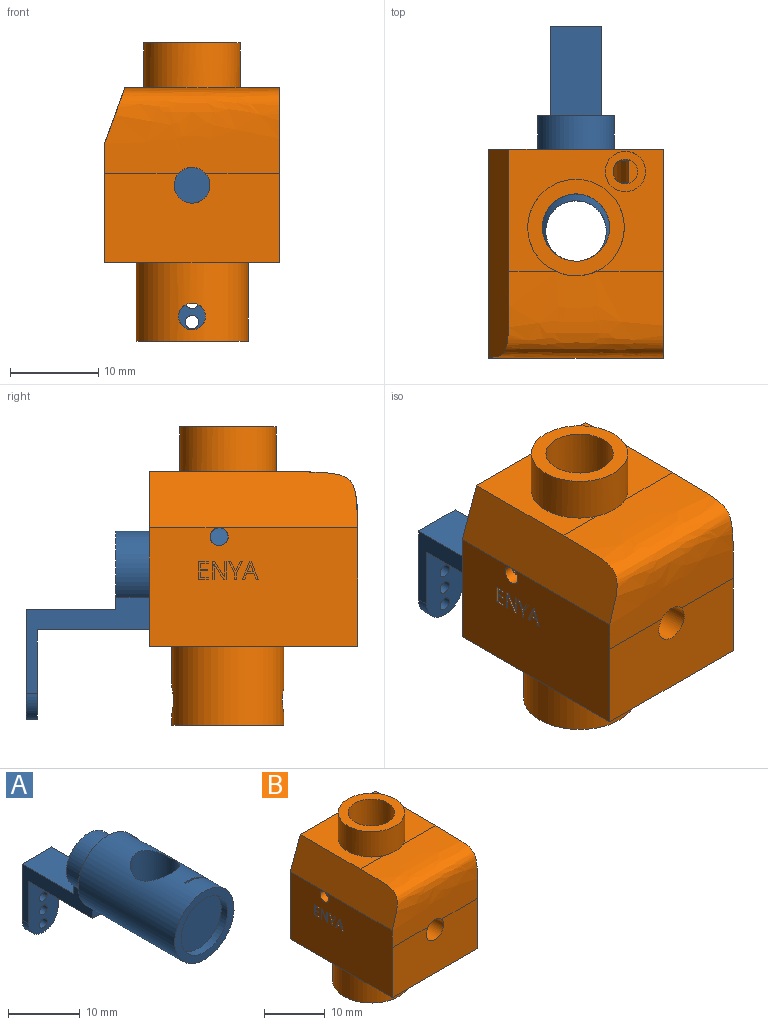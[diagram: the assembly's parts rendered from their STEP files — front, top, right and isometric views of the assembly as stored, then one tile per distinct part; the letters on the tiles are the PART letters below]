
ASSEMBLY  parts=2 mates=1
PART A: 29 faces, bbox 11.7x33x22.9 mm
  f0: cylinder r=4.32mm len=8.64mm, axis (0,-1,0), area 78.9mm2, adj f1,f17,f24,f25
  f1: plane 11.68x10.9mm, normal (0,1,0), area 39.1mm2, adj f0,f16,f24,f25
  f2: plane 11.68x11.68mm, normal (0,-1,0), area 41.6mm2, adj f3,f16
  f3: cylinder r=4.57mm len=9.14mm, axis (0,-1,0), area 36.5mm2, adj f2,f4
  f4: plane 9.14x9.14mm, normal (0,-1,0), area 65.7mm2, adj f3
  f5: cylinder r=3.43mm len=11.68mm, axis (0,0,1), area 228.4mm2, adj f16
  f6: plane 9.64x2.54mm, normal (0,-1,0), area 17.2mm2, adj f8,f16
  f7: plane 9.64x2.54mm, normal (0,1,0), area 17.2mm2, adj f8,f16
  f8: plane 9.64x2.54mm, normal (1,0,0), area 24.5mm2, adj f6,f7,f16
  f9: plane 6.21x4.58mm, normal (0,-1,0), area 21.8mm2, adj f10,f15,f16
  f10: cylinder r=1.27mm len=6.35mm, axis (1,0,0), area 23.5mm2, adj f9,f11,f15,f16
  f11: plane 6.21x4.58mm, normal (0,-1,0), area 21.8mm2, adj f10,f15,f16
  f12: plane 6.21x4.58mm, normal (0,1,0), area 21.8mm2, adj f13,f15,f16
  f13: cylinder r=1.27mm len=6.35mm, axis (1,0,0), area 23.5mm2, adj f12,f14,f15,f16
  f14: plane 6.21x4.58mm, normal (0,1,0), area 21.8mm2, adj f13,f15,f16
  f15: plane 11.64x2.54mm, normal (1,0,0), area 7.4mm2, adj f9,f10,f11,f12,f13,f14,f16
  f16: cylinder r=5.84mm len=19.05mm, axis (0,-1,0), area 583.5mm2, adj f1,f2,f5,f6,f7,f8,f9,f10
  f17: plane 8.89x8.64mm, normal (0,1,0), area 62.1mm2, adj f0,f20,f24,f25
  f18: plane 5.84x1.8mm, normal (0,-1,0), area 7.4mm2, adj f16,f19,f24,f25
  f19: plane 12.7x5.84mm, normal (0,0,-1), area 74.2mm2, adj f18,f21,f24,f25
  f20: plane 10.16x5.84mm, normal (0,0,1), area 59.4mm2, adj f17,f22,f24,f25
  f21: plane 10.16x5.84mm, normal (0,-1,0), area 50.2mm2, adj f19,f23,f24,f25,f26,f27,f28
  f22: plane 12.45x5.84mm, normal (0,1,0), area 63.6mm2, adj f20,f23,f24,f25,f26,f27,f28
  f23: cylinder r=2.92mm len=5.84mm, axis (0,-1,0), area 11.7mm2, adj f21,f22,f24,f25
  f24: plane 13.97x10.92mm, normal (1,0,0), area 46.4mm2, adj f0,f1,f17,f18,f19,f20,f21,f22
  f25: plane 13.97x10.92mm, normal (-1,0,0), area 46.4mm2, adj f0,f1,f17,f18,f19,f20,f21,f22
  f26: cylinder r=0.76mm len=1.52mm, axis (0,1,0), area 6.1mm2, adj f21,f22
  f27: cylinder r=0.76mm len=1.52mm, axis (0,1,0), area 6.1mm2, adj f21,f22
  f28: cylinder r=0.76mm len=1.52mm, axis (0,1,0), area 6.1mm2, adj f21,f22
PART B: 85 faces, bbox 24.5x26.4x36.5 mm
  f0: plane 23.68x13.52mm, normal (-1,0,0), area 310.2mm2, adj f9,f11,f13,f28,f29,f30,f31,f32
  f1: cylinder r=5.97mm len=20.32mm, axis (0,1,0), area 639mm2, adj f2,f6,f11,f16,f20,f21,f22,f23
  f2: cylinder r=3.81mm len=11.53mm, axis (0,0,-1), area 259.1mm2, adj f1,f15,f27
  f3: plane 12.7x12.7mm, normal (0,0,-1), area 19.5mm2, adj f7,f8
  f4: cylinder r=1.52mm len=3.05mm, axis (0,-1,0), area 25mm2, adj f6,f7,f8
  f5: cylinder r=1.52mm len=3.05mm, axis (0,-1,0), area 25mm2, adj f6,f7,f8
  f6: cylinder r=3.81mm len=11.03mm, axis (0,0,-1), area 251.9mm2, adj f1,f4,f5,f8
  f7: cylinder r=6.35mm len=12.7mm, axis (0,0,1), area 340mm2, adj f3,f4,f5,f9
  f8: cone r=5.84mm half-angle=45deg, axis (0,0,-1), area 84mm2, adj f3,f4,f5,f6
  f9: plane 23.62x19.81mm, normal (0,0,-1), area 341.3mm2, adj f0,f7,f11,f12,f13
  f10: plane 17.5x13.87mm, normal (0,0,1), area 134.1mm2, adj f11,f12,f14,f18,f83,f84
  f11: plane 19.81x19.81mm, normal (0,1,0), area 267.1mm2, adj f0,f1,f9,f10,f12,f25,f83
  f12: plane 25.49x21.68mm, normal (1,0,0), area 464.9mm2, adj f9,f10,f11,f13,f84
  f13: plane 19.81x10.06mm, normal (0,-1,0), area 188mm2, adj f0,f9,f12,f17,f84
  f14: cylinder r=5.46mm len=10.92mm, axis (0,0,-1), area 174.3mm2, adj f10,f15,f84
  f15: plane 10.92x10.92mm, normal (0,0,1), area 48.1mm2, adj f2,f14
  f16: plane 11.94x11.8mm, normal (0,1,0), area 96.5mm2, adj f1,f17,f23
  f17: cylinder r=2.03mm len=4.06mm, axis (0,1,0), area 42.2mm2, adj f13,f16,f84
  f18: cylinder r=2.29mm len=4.57mm, axis (0,0,1), area 25.5mm2, adj f10,f19
  f19: plane 4.57x4.57mm, normal (0,0,1), area 10.3mm2, adj f18,f21
  f20: plane 2.72x1.08mm, normal (0,0,1), area 2.2mm2, adj f1,f21
  f21: cylinder r=1.4mm len=8.38mm, axis (0,0,1), area 61.2mm2, adj f1,f19,f20
  f22: plane 2.54x1.41mm, normal (0,-1,0), area 2.6mm2, adj f1,f23
  f23: cylinder r=1.27mm len=5.33mm, axis (0,-1,0), area 23.7mm2, adj f1,f16,f22,f24
  f24: plane 2.54x2.54mm, normal (0,1,0), area 5.1mm2, adj f23
  f25: cylinder r=1.4mm len=18.29mm, axis (0,1,0), area 154.2mm2, adj f11,f26,f27,f28
  f26: plane 2.79x2.79mm, normal (0,1,0), area 6.1mm2, adj f25
  f27: cylinder r=1.02mm len=2.88mm, axis (-1,0,0), area 10.1mm2, adj f1,f2,f25
  f28: cylinder r=1.02mm len=2.03mm, axis (-1,0,0), area 8.3mm2, adj f0,f25
  f29: plane 1.27x0.27mm, normal (0,0,1), area 0.3mm2, adj f0,f30,f43,f44
  f30: plane 2.02x1.27mm, normal (0,1,0), area 2.6mm2, adj f0,f29,f31,f44
  f31: plane 1.27x0.22mm, normal (0,0,-1), area 0.3mm2, adj f0,f30,f32,f44
  f32: plane 1.27x1.16mm, normal (0,-1,0), area 1.5mm2, adj f0,f31,f33,f44
  f33: extruded ~1.27x0.29mm, area 0.4mm2, adj f0,f32,f34,f44
  f34: extruded ~1.27x0.24mm, area 0.3mm2, adj f0,f33,f35,f44
  f35: plane 1.27x0.01mm, normal (0,0,-1), area 0mm2, adj f0,f34,f36,f44
  f36: plane 1.68x1.27mm, normal (0,0.84,-0.55), area 2.6mm2, adj f0,f35,f37,f44
  f37: plane 1.27x0.26mm, normal (0,0,-1), area 0.3mm2, adj f0,f36,f38,f44
  f38: plane 2.02x1.27mm, normal (0,-1,0), area 2.6mm2, adj f0,f37,f39,f44
  f39: plane 1.27x0.22mm, normal (0,0,1), area 0.3mm2, adj f0,f38,f40,f44
  f40: plane 1.27x1.15mm, normal (0,1,0), area 1.5mm2, adj f0,f39,f41,f44
  f41: extruded ~1.27x0.55mm, area 0.7mm2, adj f0,f40,f42,f44
  f42: plane 1.27x0.01mm, normal (0,0,1), area 0mm2, adj f0,f41,f43,f44
  f43: plane 1.69x1.27mm, normal (0,-0.84,0.55), area 2.6mm2, adj f0,f29,f42,f44
  f44: plane 2.02x1.57mm, normal (-1,0,0), area 1.3mm2, adj f29,f30,f31,f32,f33,f34,f35,f36
  f45: plane 1.27x1.01mm, normal (0,-0.88,-0.47), area 1.5mm2, adj f0,f46,f53,f54
  f46: plane 1.27x1.01mm, normal (0,0.88,-0.47), area 1.4mm2, adj f0,f45,f47,f54
  f47: plane 1.27x0.26mm, normal (0,0,-1), area 0.3mm2, adj f0,f46,f48,f54
  f48: plane 1.27x1.24mm, normal (0,-0.88,0.47), area 1.8mm2, adj f0,f47,f49,f54
  f49: plane 1.27x0.77mm, normal (0,-1,0), area 1mm2, adj f0,f48,f50,f54
  f50: plane 1.27x0.24mm, normal (0,0,1), area 0.3mm2, adj f0,f49,f51,f54
  f51: plane 1.27x0.78mm, normal (0,1,0), area 1mm2, adj f0,f50,f52,f54
  f52: plane 1.27x1.23mm, normal (0,0.88,0.48), area 1.8mm2, adj f0,f51,f53,f54
  f53: plane 1.27x0.25mm, normal (0,0,-1), area 0.3mm2, adj f0,f45,f52,f54
  f54: plane 2.02x1.58mm, normal (-1,0,0), area 0.8mm2, adj f45,f46,f47,f48,f49,f50,f51,f52
  f55: plane 1.27x0.62mm, normal (0,-0.94,0.35), area 0.8mm2, adj f56,f67,f68,f82
  f56: plane 1.27x0.65mm, normal (0,0,-1), area 0.8mm2, adj f55,f57,f68,f82
  f57: plane 1.27x0.62mm, normal (0,0.94,0.35), area 0.8mm2, adj f56,f58,f68,f82
  f58: extruded ~1.27x0.29mm, area 0.4mm2, adj f57,f67,f68,f82
  f59: plane 1.27x0.64mm, normal (0,-0.93,0.36), area 0.9mm2, adj f0,f60,f66,f68
  f60: plane 1.27x0.24mm, normal (0,0,1), area 0.3mm2, adj f0,f59,f61,f68
  f61: plane 2.02x1.27mm, normal (0,0.93,-0.36), area 2.8mm2, adj f0,f60,f62,f68
  f62: plane 1.27x0.2mm, normal (0,0,-1), area 0.3mm2, adj f0,f61,f63,f68
  f63: plane 2.02x1.27mm, normal (0,-0.93,-0.37), area 2.8mm2, adj f0,f62,f64,f68
  f64: plane 1.27x0.24mm, normal (0,0,1), area 0.3mm2, adj f0,f63,f65,f68
  f65: plane 1.27x0.64mm, normal (0,0.93,0.36), area 0.9mm2, adj f0,f64,f66,f68
  f66: plane 1.27x0.81mm, normal (0,0,1), area 1mm2, adj f0,f59,f65,f68
  f67: extruded ~1.27x0.29mm, area 0.4mm2, adj f55,f58,f68,f82
  f68: plane 2.02x1.79mm, normal (-1,0,0), area 1mm2, adj f55,f56,f57,f58,f59,f60,f61,f62
  f69: plane 1.27x1.12mm, normal (0,0,1), area 1.4mm2, adj f0,f70,f80,f81
  f70: plane 1.27x0.21mm, normal (0,1,0), area 0.3mm2, adj f0,f69,f71,f81
  f71: plane 1.27x0.89mm, normal (0,0,-1), area 1.1mm2, adj f0,f70,f72,f81
  f72: plane 1.27x0.74mm, normal (0,1,0), area 0.9mm2, adj f0,f71,f73,f81
  f73: plane 1.27x0.84mm, normal (0,0,1), area 1.1mm2, adj f0,f72,f74,f81
  f74: plane 1.27x0.21mm, normal (0,1,0), area 0.3mm2, adj f0,f73,f75,f81
  f75: plane 1.27x0.84mm, normal (0,0,-1), area 1.1mm2, adj f0,f74,f76,f81
  f76: plane 1.27x0.65mm, normal (0,1,0), area 0.8mm2, adj f0,f75,f77,f81
  f77: plane 1.27x0.89mm, normal (0,0,1), area 1.1mm2, adj f0,f76,f78,f81
  f78: plane 1.27x0.21mm, normal (0,1,0), area 0.3mm2, adj f0,f77,f79,f81
  f79: plane 1.27x1.12mm, normal (0,0,-1), area 1.4mm2, adj f0,f78,f80,f81
  f80: plane 2.02x1.27mm, normal (0,-1,0), area 2.6mm2, adj f0,f69,f79,f81
  f81: plane 2.02x1.12mm, normal (-1,0,0), area 1mm2, adj f69,f70,f71,f72,f73,f74,f75,f76
  f82: plane 0.92x0.65mm, normal (-1,0,0), area 0.3mm2, adj f55,f56,f57,f58,f67
  f83: plane 26.35x9.08mm, normal (-0.94,0,0.34), area 156.3mm2, adj f0,f10,f11,f84
  f84: bspline ~21.79x9.75mm, area 337.6mm2, adj f0,f10,f12,f13,f14,f17,f83
PLACE A rot(axis=(0,-1,0),0deg) t=(-21.51,4.03,-3.32)mm
PLACE B t=(-21.51,2.76,-3.32)mm fixed
MATE revolute A.f16 <-> B.f1  axis (0,-1,0) through (-21.51,2.13,14.33)mm
